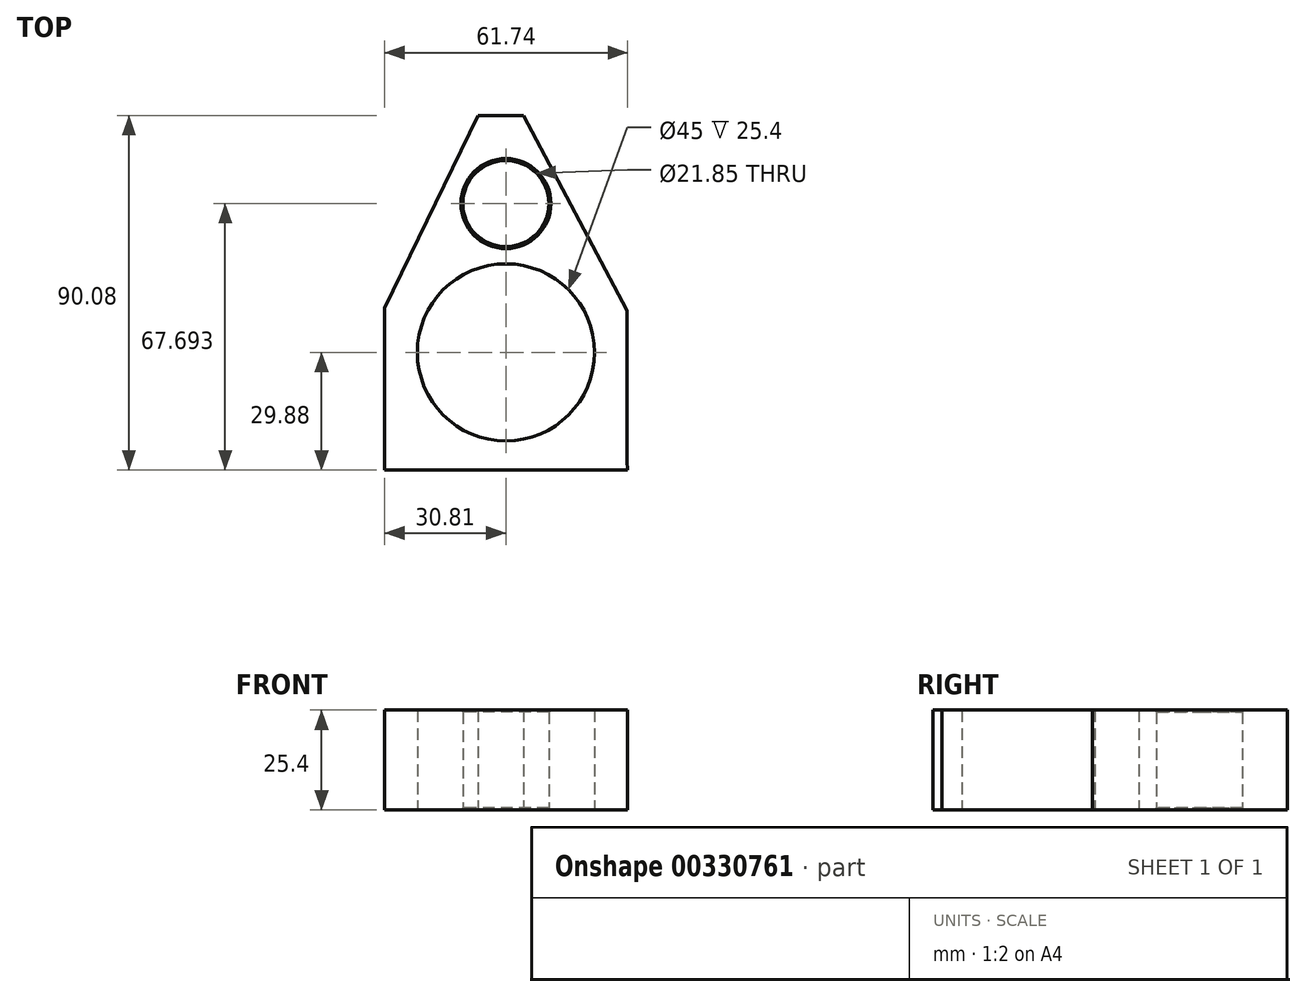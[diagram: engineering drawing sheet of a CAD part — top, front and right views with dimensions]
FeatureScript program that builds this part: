
annotation { "Feature Type Name" : "Feature", "Feature Type Description" : "" }
export const myFeature = defineFeature(function(context is Context, id is Id, definition is map)
    precondition{}
    {
        {
            var Q0;
            Q0=qCreatedBy(makeId("Top.planeOp"),FACE);
            var sketch = newSketch(context, id + "F0", { "sketchPlane" : qUnion([Q0])});
            skLineSegment(sketch, "E0.top", {"start": v(4.52, 60.2) * mm, "end": v(-7.05, 60.2) * mm});
            skLineSegment(sketch, "E0.left", {"start": v(30.8, -27.64) * mm, "end": v(30.8, 10.6) * mm});
            skLineSegment(sketch, "E0.right", {"start": v(-30.8, -23.55) * mm, "end": v(-30.8, 11.29) * mm});
            skPoint(sketch, "E0.middle", {"position": v(0, 0) * mm});
            skCircle(sketch, "E1", {"center": v(0, 0) * mm, "radius": 22.5 * mm});
            skCircle(sketch, "E2", {"center": v(0, 37.81) * mm, "radius": 10.93 * mm});
            skLineSegment(sketch, "E3", {"start": v(30.93, -29.88) * mm, "end": v(30.8, -27.64) * mm});
            skPoint(sketch, "E4.orphan", {"position": v(-30.8, -60.2) * mm});
            skPoint(sketch, "E5.orphan", {"position": v(-30.8, 60.2) * mm});
            skPoint(sketch, "E6.orphan", {"position": v(30.8, 60.2) * mm});
            skPoint(sketch, "E7.orphan", {"position": v(30.8, -60.2) * mm});
            skLineSegment(sketch, "E8", {"start": v(-26.06, -29.88) * mm, "end": v(30.93, -29.88) * mm});
            skLineSegment(sketch, "E9", {"start": v(4.52, 60.2) * mm, "end": v(30.8, 10.6) * mm});
            skPoint(sketch, "E10.orphan", {"position": v(30.8, 48.85) * mm});
            skLineSegment(sketch, "E11", {"start": v(-7.05, 60.2) * mm, "end": v(-30.8, 11.29) * mm});
            skLineSegment(sketch, "E12", {"start": v(-30.8, -23.55) * mm, "end": v(-30.8, -29.85) * mm});
            skLineSegment(sketch, "E13", {"start": v(-30.8, -29.85) * mm, "end": v(-26.06, -29.88) * mm});
            skSolve(sketch);
        }
        {
            var Q0;
            Q0=qSketchRegion(id+"F0",true);
            extrude(context, id + "F1", {"entities" : qUnion([Q0]), "depth" : 25.4 * mm});
        }
        {
            var Q0;
            Q0=makeQuery(id+"F1.opExtrude","CAP_EDGE",EDGE,{"disambiguationData":[OSD([sQuery(id+"F0.wireOp",EDGE,"E2")])],"isStart":true});
            chamfer(context, id + "F2", {"entities" : qUnion([Q0]), "width" : 0.5 * mm, "tangentPropagation" : true});
        }
        {
            var Q0;
            Q0=makeQuery(id+"F1.opExtrude","CAP_EDGE",EDGE,{"disambiguationData":[OSD([sQuery(id+"F0.wireOp",EDGE,"E2")])],"isStart":false});
            chamfer(context, id + "F3", {"entities" : qUnion([Q0]), "width" : 0.5 * mm, "tangentPropagation" : true});
        }
    });
